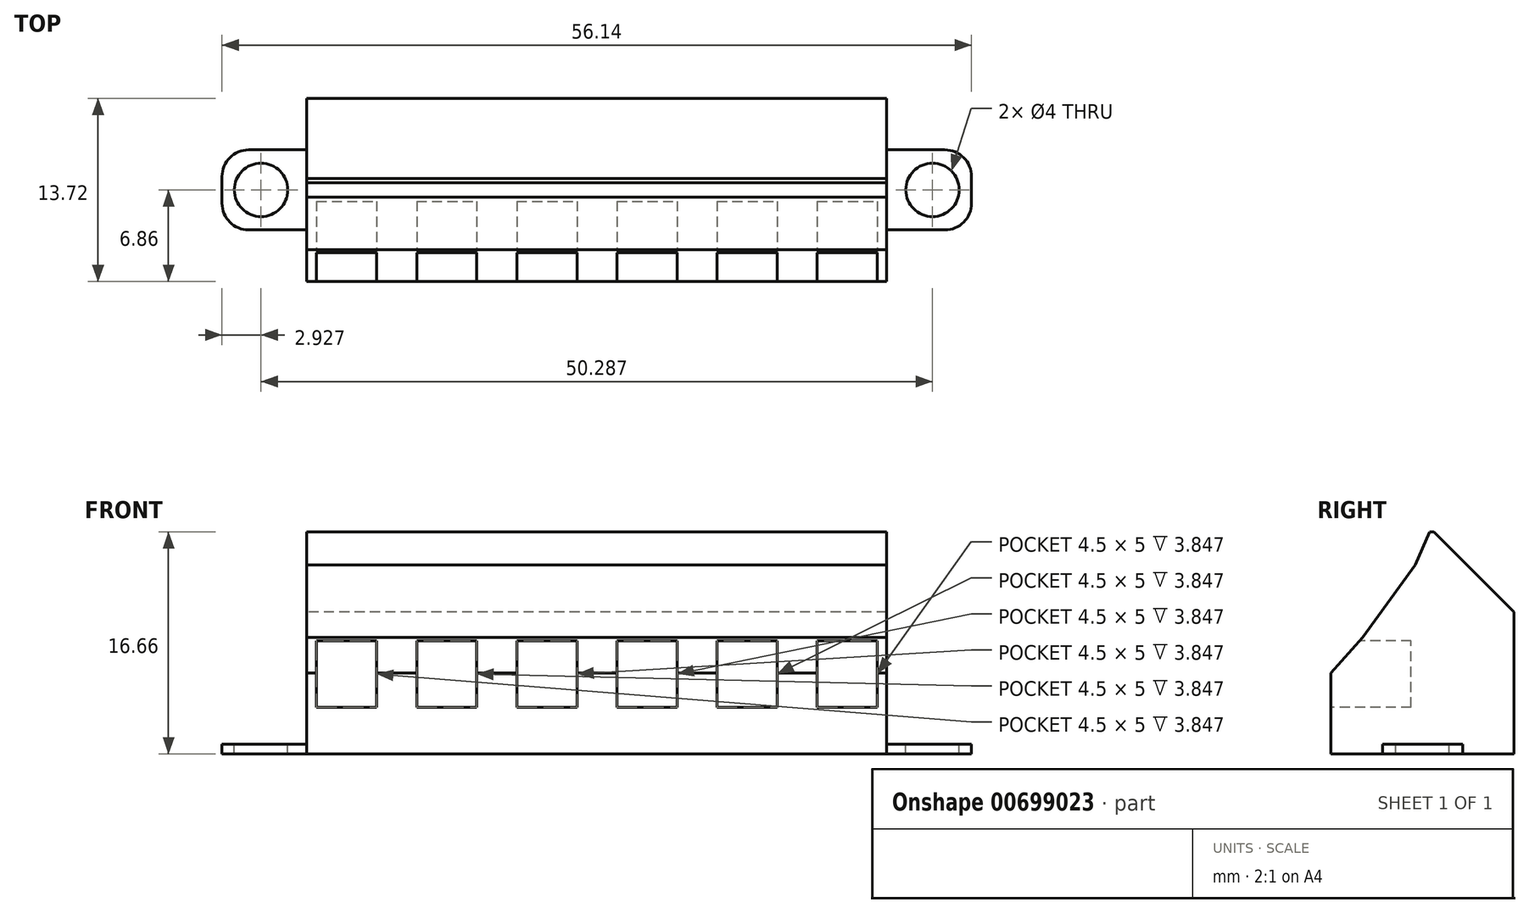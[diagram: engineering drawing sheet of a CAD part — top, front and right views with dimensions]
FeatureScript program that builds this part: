
annotation { "Feature Type Name" : "Feature", "Feature Type Description" : "" }
export const myFeature = defineFeature(function(context is Context, id is Id, definition is map)
    precondition{}
    {
        {
            var Q0;
            Q0=qCreatedBy(makeId("Top.planeOp"),FACE);
            var sketch = newSketch(context, id + "F0", { "sketchPlane" : qUnion([Q0])});
            skLineSegment(sketch, "E0.bottom", {"start": v(21.72, -6.86) * mm, "end": v(-21.72, -6.86) * mm});
            skLineSegment(sketch, "E0.top", {"start": v(21.72, 6.86) * mm, "end": v(-21.72, 6.86) * mm});
            skLineSegment(sketch, "E0.left", {"start": v(21.72, -6.86) * mm, "end": v(21.72, 6.86) * mm});
            skLineSegment(sketch, "E0.right", {"start": v(-21.72, -6.86) * mm, "end": v(-21.72, 6.86) * mm});
            skPoint(sketch, "E0.middle", {"position": v(0, 0) * mm});
            skSolve(sketch);
        }
        {
            var Q0;
            Q0=qSketchRegion(id+"F0",true);
            extrude(context, id + "F1", {"entities" : qUnion([Q0]), "depth" : 16.66 * mm, "offsetDistance" : 25 * mm});
        }
        {
            var Q0;
            Q0=makeQuery(id+"F1.opExtrude","SWEPT_FACE",FACE,{"disambiguationData":[OSD([sQuery(id+"F0.wireOp",EDGE,"E0.right")])]});
            var sketch = newSketch(context, id + "F2", { "sketchPlane" : qUnion([Q0])});
            skLineSegment(sketch, "E1", {"start": v(-0.86, 16.66) * mm, "end": v(-6.86, 10.66) * mm});
            skLineSegment(sketch, "E2", {"start": v(-0.53, 16.66) * mm, "end": v(0.54, 14.16) * mm});
            skLineSegment(sketch, "E3", {"start": v(0.54, 14.16) * mm, "end": v(4.5, 8.74) * mm});
            skLineSegment(sketch, "E4", {"start": v(4.5, 8.74) * mm, "end": v(6.86, 6.08) * mm});
            skSolve(sketch);
        }
        {
            var Q0;
            {var subQ0=sQuery(id+"F2.wireOp",EDGE,"E1");Q0=makeQuery(id+"F2.imprint","IMPRINT",FACE,{"disambiguationData":[TD([[makeQuery(id+"F2.imprint","IMPRINT",EDGE,{"derivedFrom":subQ0}),-1.0]])]});}
            var Q1;
            {var subQ5=sQuery(id+"F2.wireOp",EDGE,"E2");Q1=makeQuery(id+"F2.imprint","IMPRINT",FACE,{"disambiguationData":[TD([[makeQuery(id+"F2.imprint","IMPRINT",EDGE,{"derivedFrom":subQ5}),1.0]])]});}
            extrude(context, id + "F3", {"entities" : qUnion([Q0, Q1]), "operationType" : NewBodyOperationType.REMOVE, "endBound" : BoundingType.THROUGH_ALL, "oppositeDirection" : true, "depth" : 25 * mm, "offsetDistance" : 25 * mm});
        }
        {
            var Q0;
            Q0=makeQuery(id+"F1.opExtrude","SWEPT_FACE",FACE,{"disambiguationData":[OSD([sQuery(id+"F0.wireOp",EDGE,"E0.bottom")])]});
            var sketch = newSketch(context, id + "F4", { "sketchPlane" : qUnion([Q0])});
            skLineSegment(sketch, "E5.bottom", {"start": v(-20.99, 3.5) * mm, "end": v(-16.49, 3.5) * mm});
            skLineSegment(sketch, "E5.top", {"start": v(-20.99, 8.5) * mm, "end": v(-16.49, 8.5) * mm});
            skLineSegment(sketch, "E5.left", {"start": v(-20.99, 3.5) * mm, "end": v(-20.99, 8.5) * mm});
            skLineSegment(sketch, "E5.right", {"start": v(-16.49, 3.5) * mm, "end": v(-16.49, 8.5) * mm});
            skLineSegment(sketch, "E6.1.0.0", {"start": v(-13.49, 3.5) * mm, "end": v(-8.99, 3.5) * mm});
            skLineSegment(sketch, "E6.1.0.1", {"start": v(-13.49, 3.5) * mm, "end": v(-13.49, 8.5) * mm});
            skLineSegment(sketch, "E6.1.0.2", {"start": v(-8.99, 3.5) * mm, "end": v(-8.99, 8.5) * mm});
            skLineSegment(sketch, "E6.1.0.3", {"start": v(-13.49, 8.5) * mm, "end": v(-8.99, 8.5) * mm});
            skLineSegment(sketch, "E6.2.0.0", {"start": v(-5.99, 3.5) * mm, "end": v(-1.49, 3.5) * mm});
            skLineSegment(sketch, "E6.2.0.1", {"start": v(-5.99, 3.5) * mm, "end": v(-5.99, 8.5) * mm});
            skLineSegment(sketch, "E6.2.0.2", {"start": v(-1.49, 3.5) * mm, "end": v(-1.49, 8.5) * mm});
            skLineSegment(sketch, "E6.2.0.3", {"start": v(-5.99, 8.5) * mm, "end": v(-1.49, 8.5) * mm});
            skLineSegment(sketch, "E6.3.0.0", {"start": v(1.51, 3.5) * mm, "end": v(6.01, 3.5) * mm});
            skLineSegment(sketch, "E6.3.0.1", {"start": v(1.51, 3.5) * mm, "end": v(1.51, 8.5) * mm});
            skLineSegment(sketch, "E6.3.0.2", {"start": v(6.01, 3.5) * mm, "end": v(6.01, 8.5) * mm});
            skLineSegment(sketch, "E6.3.0.3", {"start": v(1.51, 8.5) * mm, "end": v(6.01, 8.5) * mm});
            skLineSegment(sketch, "E6.4.0.0", {"start": v(9.01, 3.5) * mm, "end": v(13.51, 3.5) * mm});
            skLineSegment(sketch, "E6.4.0.1", {"start": v(9.01, 3.5) * mm, "end": v(9.01, 8.5) * mm});
            skLineSegment(sketch, "E6.4.0.2", {"start": v(13.51, 3.5) * mm, "end": v(13.51, 8.5) * mm});
            skLineSegment(sketch, "E6.4.0.3", {"start": v(9.01, 8.5) * mm, "end": v(13.51, 8.5) * mm});
            skLineSegment(sketch, "E6.5.0.0", {"start": v(16.51, 3.5) * mm, "end": v(21.01, 3.5) * mm});
            skLineSegment(sketch, "E6.5.0.1", {"start": v(16.51, 3.5) * mm, "end": v(16.51, 8.5) * mm});
            skLineSegment(sketch, "E6.5.0.2", {"start": v(21.01, 3.5) * mm, "end": v(21.01, 8.5) * mm});
            skLineSegment(sketch, "E6.5.0.3", {"start": v(16.51, 8.5) * mm, "end": v(21.01, 8.5) * mm});
            skLineSegment(sketch, "E6.6.0.0", {"start": v(24.01, 3.5) * mm, "end": v(28.51, 3.5) * mm});
            skLineSegment(sketch, "E6.6.0.1", {"start": v(24.01, 3.5) * mm, "end": v(24.01, 8.5) * mm});
            skLineSegment(sketch, "E6.6.0.2", {"start": v(28.51, 3.5) * mm, "end": v(28.51, 8.5) * mm});
            skLineSegment(sketch, "E6.6.0.3", {"start": v(24.01, 8.5) * mm, "end": v(28.51, 8.5) * mm});
            skLineSegment(sketch, "E6.7.0.0", {"start": v(31.51, 3.5) * mm, "end": v(36.01, 3.5) * mm});
            skLineSegment(sketch, "E6.7.0.1", {"start": v(31.51, 3.5) * mm, "end": v(31.51, 8.5) * mm});
            skLineSegment(sketch, "E6.7.0.2", {"start": v(36.01, 3.5) * mm, "end": v(36.01, 8.5) * mm});
            skLineSegment(sketch, "E6.7.0.3", {"start": v(31.51, 8.5) * mm, "end": v(36.01, 8.5) * mm});
            skLineSegment(sketch, "E6.8.0.0", {"start": v(39.01, 3.5) * mm, "end": v(43.51, 3.5) * mm});
            skLineSegment(sketch, "E6.8.0.1", {"start": v(39.01, 3.5) * mm, "end": v(39.01, 8.5) * mm});
            skLineSegment(sketch, "E6.8.0.2", {"start": v(43.51, 3.5) * mm, "end": v(43.51, 8.5) * mm});
            skLineSegment(sketch, "E6.8.0.3", {"start": v(39.01, 8.5) * mm, "end": v(43.51, 8.5) * mm});
            skLineSegment(sketch, "E6.9.0.0", {"start": v(46.51, 3.5) * mm, "end": v(51.01, 3.5) * mm});
            skLineSegment(sketch, "E6.9.0.1", {"start": v(46.51, 3.5) * mm, "end": v(46.51, 8.5) * mm});
            skLineSegment(sketch, "E6.9.0.2", {"start": v(51.01, 3.5) * mm, "end": v(51.01, 8.5) * mm});
            skLineSegment(sketch, "E6.9.0.3", {"start": v(46.51, 8.5) * mm, "end": v(51.01, 8.5) * mm});
            skLineSegment(sketch, "E6.10.0.0", {"start": v(54.01, 3.5) * mm, "end": v(58.51, 3.5) * mm});
            skLineSegment(sketch, "E6.10.0.1", {"start": v(54.01, 3.5) * mm, "end": v(54.01, 8.5) * mm});
            skLineSegment(sketch, "E6.10.0.2", {"start": v(58.51, 3.5) * mm, "end": v(58.51, 8.5) * mm});
            skLineSegment(sketch, "E6.10.0.3", {"start": v(54.01, 8.5) * mm, "end": v(58.51, 8.5) * mm});
            skLineSegment(sketch, "E6.11.0.0", {"start": v(61.51, 3.5) * mm, "end": v(66.01, 3.5) * mm});
            skLineSegment(sketch, "E6.11.0.1", {"start": v(61.51, 3.5) * mm, "end": v(61.51, 8.5) * mm});
            skLineSegment(sketch, "E6.11.0.2", {"start": v(66.01, 3.5) * mm, "end": v(66.01, 8.5) * mm});
            skLineSegment(sketch, "E6.11.0.3", {"start": v(61.51, 8.5) * mm, "end": v(66.01, 8.5) * mm});
            skLineSegment(sketch, "E6.direction1", {"start": v(-20.99, 3.5) * mm, "end": v(-13.49, 3.5) * mm, "construction": true});
            skSolve(sketch);
        }
        {
            var Q0;
            Q0=qSketchRegion(id+"F4",true);
            var Q1;
            Q1=qSketchRegion(id+"FMBLiazpq1kLS5e_1",true);
            extrude(context, id + "F5", {"entities" : qUnion([Q0, Q1]), "operationType" : NewBodyOperationType.REMOVE, "oppositeDirection" : true, "depth" : 6 * mm, "offsetDistance" : 25 * mm});
        }
        {
            var Q0;
            Q0=makeQuery(id+"F3.boolean.opBoolean","COPY",FACE,{"derivedFrom":makeQuery(id+"F3.opExtrude","SWEPT_FACE",FACE,{"disambiguationData":[OSD([sQuery(id+"F2.wireOp",EDGE,"E1")])]})});
            var sketch = newSketch(context, id + "F6", { "sketchPlane" : qUnion([Q0])});
            skCircle(sketch, "E7", {"center": v(-18.74, -6.93) * mm, "radius": 2.25 * mm});
            skCircle(sketch, "E8.1.0.0", {"center": v(-11.24, -6.93) * mm, "radius": 2.25 * mm});
            skCircle(sketch, "E8.2.0.0", {"center": v(-3.74, -6.93) * mm, "radius": 2.25 * mm});
            skCircle(sketch, "E8.3.0.0", {"center": v(3.76, -6.93) * mm, "radius": 2.25 * mm});
            skCircle(sketch, "E8.4.0.0", {"center": v(11.26, -6.93) * mm, "radius": 2.25 * mm});
            skCircle(sketch, "E8.5.0.0", {"center": v(18.76, -6.93) * mm, "radius": 2.25 * mm});
            skCircle(sketch, "E8.6.0.0", {"center": v(26.26, -6.93) * mm, "radius": 2.25 * mm});
            skCircle(sketch, "E8.7.0.0", {"center": v(33.76, -6.93) * mm, "radius": 2.25 * mm});
            skCircle(sketch, "E8.8.0.0", {"center": v(41.26, -6.93) * mm, "radius": 2.25 * mm});
            skCircle(sketch, "E8.9.0.0", {"center": v(48.76, -6.93) * mm, "radius": 2.25 * mm});
            skCircle(sketch, "E8.10.0.0", {"center": v(56.26, -6.93) * mm, "radius": 2.25 * mm});
            skCircle(sketch, "E8.11.0.0", {"center": v(63.76, -6.93) * mm, "radius": 2.25 * mm});
            skLineSegment(sketch, "E8.direction1", {"start": v(-18.74, -6.93) * mm, "end": v(-11.24, -6.93) * mm, "construction": true});
            skSolve(sketch);
        }
        {
            var Q0;
            Q0=qSketchRegion(id+"F6",true);
            extrude(context, id + "F7", {"entities" : qUnion([Q0]), "operationType" : NewBodyOperationType.REMOVE, "oppositeDirection" : true, "depth" : 2 * mm, "offsetDistance" : 25 * mm});
        }
        {
            var Q0;
            Q0=makeQuery(id+"F1.opExtrude","SWEPT_FACE",FACE,{"disambiguationData":[OSD([sQuery(id+"F0.wireOp",EDGE,"E0.right")])]});
            var sketch = newSketch(context, id + "F8", { "sketchPlane" : qUnion([Q0])});
            skLineSegment(sketch, "E9.bottom", {"start": v(3, 0.75) * mm, "end": v(-3, 0.75) * mm});
            skLineSegment(sketch, "E9.top", {"start": v(3, -0.75) * mm, "end": v(-3, -0.75) * mm});
            skLineSegment(sketch, "E9.left", {"start": v(3, 0.75) * mm, "end": v(3, -0.75) * mm});
            skLineSegment(sketch, "E9.right", {"start": v(-3, 0.75) * mm, "end": v(-3, -0.75) * mm});
            skPoint(sketch, "E9.middle", {"position": v(0, 0) * mm});
            skSolve(sketch);
        }
        {
            var Q0;
            {var subQ0=sQuery(id+"F8.wireOp",EDGE,"E9.bottom");Q0=makeQuery(id+"F8.imprint","IMPRINT",FACE,{"disambiguationData":[TD([[makeQuery(id+"F8.imprint","IMPRINT",EDGE,{"derivedFrom":subQ0}),1.0]])]});}
            extrude(context, id + "F9", {"entities" : qUnion([Q0]), "operationType" : NewBodyOperationType.ADD, "depth" : 6.35 * mm, "offsetDistance" : 25 * mm});
        }
        {
            var Q0;
            Q0=makeQuery(id+"F1.opExtrude","SWEPT_FACE",FACE,{"disambiguationData":[OSD([sQuery(id+"F0.wireOp",EDGE,"E0.left")])]});
            var sketch = newSketch(context, id + "F10", { "sketchPlane" : qUnion([Q0])});
            skLineSegment(sketch, "E10.bottom", {"start": v(-3, -0.75) * mm, "end": v(3, -0.75) * mm});
            skLineSegment(sketch, "E10.top", {"start": v(-3, 0.75) * mm, "end": v(3, 0.75) * mm});
            skLineSegment(sketch, "E10.left", {"start": v(-3, -0.75) * mm, "end": v(-3, 0.75) * mm});
            skLineSegment(sketch, "E10.right", {"start": v(3, -0.75) * mm, "end": v(3, 0.75) * mm});
            skPoint(sketch, "E10.middle", {"position": v(0, 0) * mm});
            skSolve(sketch);
        }
        {
            var Q0;
            {var subQ0=sQuery(id+"F10.wireOp",EDGE,"E10.top");Q0=makeQuery(id+"F10.imprint","IMPRINT",FACE,{"disambiguationData":[TD([[makeQuery(id+"F10.imprint","IMPRINT",EDGE,{"derivedFrom":subQ0}),-1.0]])]});}
            extrude(context, id + "F11", {"entities" : qUnion([Q0]), "operationType" : NewBodyOperationType.ADD, "depth" : 6.35 * mm, "offsetDistance" : 25 * mm});
        }
        {
            var Q0;
            Q0=makeQuery(id+"F9.opExtrude","CAP_EDGE",EDGE,{"disambiguationData":[OSD([sQuery(id+"F8.wireOp",EDGE,"E9.right")])],"isStart":false});
            var Q1;
            Q1=makeQuery(id+"F9.opExtrude","CAP_EDGE",EDGE,{"disambiguationData":[OSD([sQuery(id+"F8.wireOp",EDGE,"E9.left")])],"isStart":false});
            var Q2;
            Q2=makeQuery(id+"F11.opExtrude","CAP_EDGE",EDGE,{"disambiguationData":[OSD([sQuery(id+"F10.wireOp",EDGE,"E10.left")])],"isStart":false});
            var Q3;
            Q3=makeQuery(id+"F11.opExtrude","CAP_EDGE",EDGE,{"disambiguationData":[OSD([sQuery(id+"F10.wireOp",EDGE,"E10.right")])],"isStart":false});
            fillet(context, id + "F12", {"entities" : qUnion([Q0, Q1, Q2, Q3]), "radius" : 2 * mm, "tangentPropagation" : true, "allowEdgeOverflow" : false});
        }
        {
            var Q0;
            Q0=makeQuery(id+"F9.opExtrude","SWEPT_FACE",FACE,{"disambiguationData":[OSD([sQuery(id+"F8.wireOp",EDGE,"E9.bottom")])]});
            var sketch = newSketch(context, id + "F13", { "sketchPlane" : qUnion([Q0])});
            skCircle(sketch, "E11", {"center": v(-25.14, 0) * mm, "radius": 2 * mm});
            skPoint(sketch, "E11.centerSnap0", {"position": v(-28.07, 0) * mm});
            skSolve(sketch);
        }
        {
            var Q0;
            Q0=qSketchRegion(id+"F13",true);
            extrude(context, id + "F14", {"entities" : qUnion([Q0]), "operationType" : NewBodyOperationType.REMOVE, "endBound" : BoundingType.THROUGH_ALL, "oppositeDirection" : true, "depth" : 0.5 * mm, "offsetDistance" : 25 * mm});
        }
        {
            var Q0;
            Q0=makeQuery(id+"F11.opExtrude","SWEPT_FACE",FACE,{"disambiguationData":[OSD([sQuery(id+"F10.wireOp",EDGE,"E10.top")])]});
            var sketch = newSketch(context, id + "F15", { "sketchPlane" : qUnion([Q0])});
            skCircle(sketch, "E12", {"center": v(25.14, 0) * mm, "radius": 2 * mm});
            skPoint(sketch, "E12.centerSnap0", {"position": v(28.07, 0) * mm});
            skSolve(sketch);
        }
        {
            var Q0;
            Q0=qSketchRegion(id+"F15",true);
            extrude(context, id + "F16", {"entities" : qUnion([Q0]), "operationType" : NewBodyOperationType.REMOVE, "endBound" : BoundingType.THROUGH_ALL, "oppositeDirection" : true, "depth" : 0.5 * mm, "offsetDistance" : 25 * mm});
        }
    });
